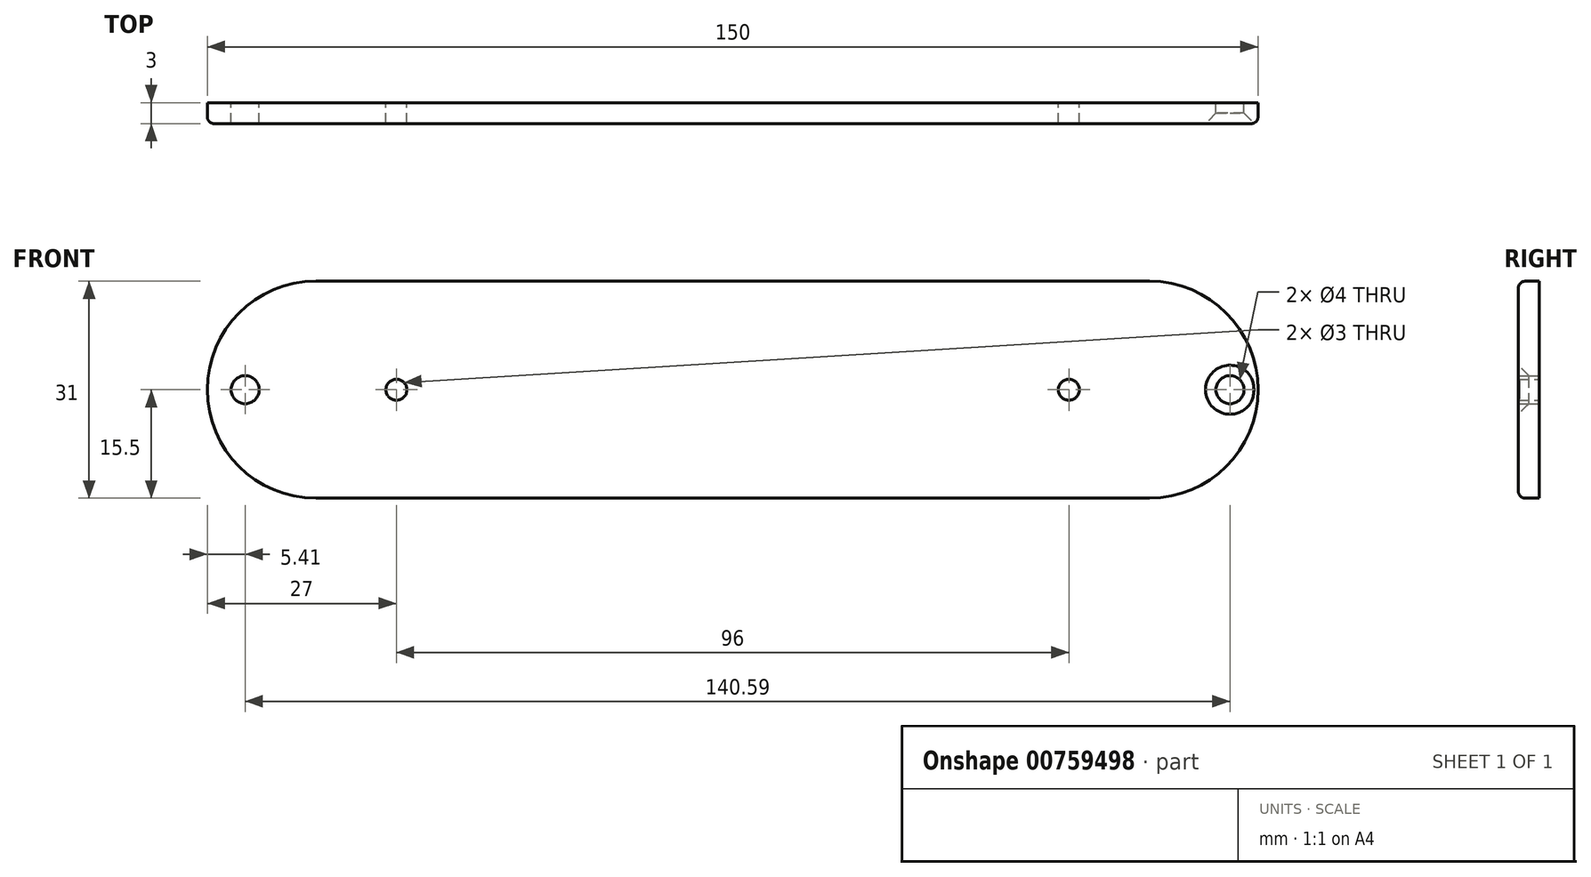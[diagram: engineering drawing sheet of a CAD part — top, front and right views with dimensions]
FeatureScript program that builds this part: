
annotation { "Feature Type Name" : "Feature", "Feature Type Description" : "" }
export const myFeature = defineFeature(function(context is Context, id is Id, definition is map)
    precondition{}
    {
        {
            var Q0;
            Q0=qCreatedBy(makeId("Front.planeOp"),FACE);
            var sketch = newSketch(context, id + "F0", { "sketchPlane" : qUnion([Q0])});
            skLineSegment(sketch, "E0.bottom", {"start": v(-59.5, 15.5) * mm, "end": v(59.5, 15.5) * mm});
            skLineSegment(sketch, "E0.top", {"start": v(-59.5, -15.5) * mm, "end": v(59.5, -15.5) * mm});
            skPoint(sketch, "E0.middle", {"position": v(0, 0) * mm});
            skArc(sketch, "E1", {"start": v(-59.5, 15.5) * mm, "mid": v(-75, 0) * mm, "end": v(-59.5, -15.5) * mm});
            skArc(sketch, "E2", {"start": v(59.5, 15.5) * mm, "mid": v(75, 0) * mm, "end": v(59.5, -15.5) * mm});
            skCircle(sketch, "E3", {"center": v(-69.6, 0) * mm, "radius": 2 * mm});
            skCircle(sketch, "E4", {"center": v(-48, 0) * mm, "radius": 1.5 * mm});
            skCircle(sketch, "E5", {"center": v(71, 0) * mm, "radius": 2 * mm});
            skCircle(sketch, "E6", {"center": v(48, 0) * mm, "radius": 1.5 * mm});
            skSolve(sketch);
        }
        {
            var Q0;
            Q0 = qSketchRegion(id + "F0", true);
            extrude(context, id + "F1", {"entities" : qUnion([Q0]), "depth" : 3 * mm, "offsetDistance" : 25 * mm});
        }
        {
            var Q0;
            Q0=makeQuery(id+"F1.opExtrude","CAP_EDGE",EDGE,{"disambiguationData":[OSD([sQuery(id+"F0.wireOp",EDGE,"E0.bottom")])],"isStart":false});
            fillet(context, id + "F2", {"entities" : qUnion([Q0]), "radius" : 1 * mm, "tangentPropagation" : true, "allowEdgeOverflow" : false});
        }
        {
            var Q0;
            Q0=makeQuery(id+"F1.opExtrude","CAP_EDGE",EDGE,{"disambiguationData":[OSD([sQuery(id+"F0.wireOp",EDGE,"E3")])],"isStart":false});
            var Q1;
            Q1=makeQuery(id+"F1.opExtrude","CAP_EDGE",EDGE,{"disambiguationData":[OSD([sQuery(id+"F0.wireOp",EDGE,"E5")])],"isStart":false});
            chamfer(context, id + "F3", {"entities" : qUnion([Q0, Q1]), "width" : 1.5 * mm, "tangentPropagation" : true});
        }
    });
